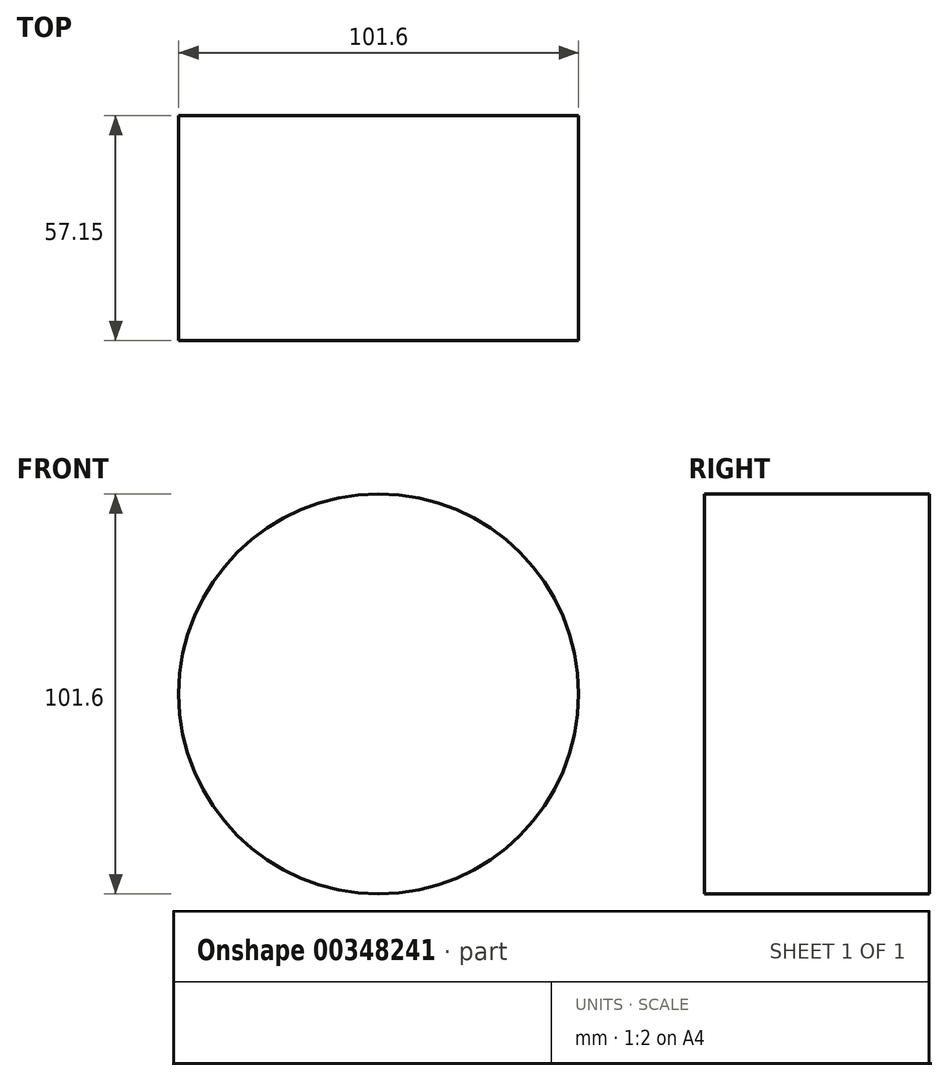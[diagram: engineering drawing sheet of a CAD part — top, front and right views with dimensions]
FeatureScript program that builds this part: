
annotation { "Feature Type Name" : "Feature", "Feature Type Description" : "" }
export const myFeature = defineFeature(function(context is Context, id is Id, definition is map)
    precondition{}
    {
        {
            var Q0;
            Q0=qCreatedBy(makeId("Front.planeOp"),FACE);
            var sketch = newSketch(context, id + "F0", { "sketchPlane" : qUnion([Q0])});
            skCircle(sketch, "E0", {"center": v(0, 0) * mm, "radius": 50.8 * mm});
            skSolve(sketch);
        }
        {
            var Q0;
            Q0=makeQuery(id+"F0.imprint","IMPRINT",FACE,{"disambiguationData":[TD([[makeQuery(id+"F0.imprint","IMPRINT",EDGE,{"derivedFrom":sQuery(id+"F0.wireOp",EDGE,"E0")}),1.0]])]});
            extrude(context, id + "F1", {"entities" : qUnion([Q0]), "oppositeDirection" : true, "depth" : 57.15 * mm});
        }
    });
